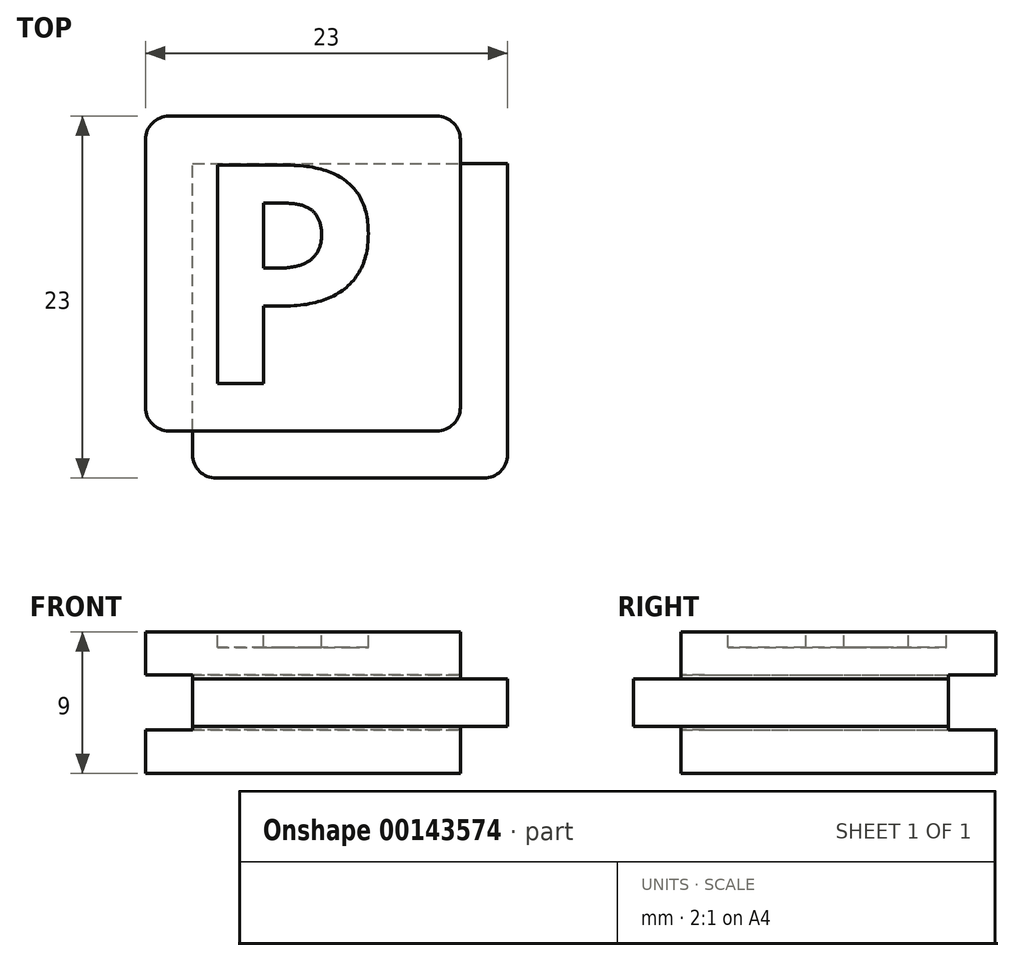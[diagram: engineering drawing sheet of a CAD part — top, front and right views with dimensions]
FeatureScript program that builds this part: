
annotation { "Feature Type Name" : "Feature", "Feature Type Description" : "" }
export const myFeature = defineFeature(function(context is Context, id is Id, definition is map)
    precondition{}
    {
        {
            var Q0;
            Q0=qCreatedBy(makeId("Front.planeOp"),FACE);
            var sketch = newSketch(context, id + "F0", { "sketchPlane" : qUnion([Q0])});
            skLineSegment(sketch, "E0.bottom", {"start": v(10, 4.5) * mm, "end": v(-10, 4.5) * mm});
            skLineSegment(sketch, "E0.top", {"start": v(10, -4.5) * mm, "end": v(-10, -4.5) * mm});
            skLineSegment(sketch, "E0.left", {"start": v(10, 4.5) * mm, "end": v(10, -4.5) * mm});
            skLineSegment(sketch, "E0.right", {"start": v(-10, 4.5) * mm, "end": v(-10, -4.5) * mm});
            skPoint(sketch, "E0.middle", {"position": v(0, 0) * mm});
            skLineSegment(sketch, "E1.bottom", {"start": v(13, 1.5) * mm, "end": v(7, 1.5) * mm});
            skLineSegment(sketch, "E1.top", {"start": v(13, -1.5) * mm, "end": v(7, -1.5) * mm});
            skLineSegment(sketch, "E1.left", {"start": v(13, 1.5) * mm, "end": v(13, -1.5) * mm});
            skLineSegment(sketch, "E1.right", {"start": v(7, 1.5) * mm, "end": v(7, -1.5) * mm});
            skPoint(sketch, "E1.middle", {"position": v(10, 0) * mm});
            skLineSegment(sketch, "E2.bottom", {"start": v(7, 1.5) * mm, "end": v(-7, 1.5) * mm});
            skLineSegment(sketch, "E2.top", {"start": v(7, -1.5) * mm, "end": v(-7, -1.5) * mm});
            skLineSegment(sketch, "E2.right", {"start": v(-7, 1.5) * mm, "end": v(-7, -1.5) * mm});
            skLineSegment(sketch, "E3.bottom", {"start": v(-7, -1.5) * mm, "end": v(-10, -1.5) * mm});
            skLineSegment(sketch, "E3.top", {"start": v(-7, 1.5) * mm, "end": v(-10, 1.5) * mm});
            skLineSegment(sketch, "E3.left", {"start": v(-7, -1.5) * mm, "end": v(-7, 1.5) * mm});
            skLineSegment(sketch, "E3.right", {"start": v(-10, -1.5) * mm, "end": v(-10, 1.5) * mm});
            skSolve(sketch);
        }
        {
            var Q0;
            {var subQ5=sQuery(id+"F0.wireOp",EDGE,"E0.bottom");Q0=makeQuery(id+"F0.imprint","IMPRINT",FACE,{"disambiguationData":[TD([[makeQuery(id+"F0.imprint","IMPRINT",EDGE,{"derivedFrom":subQ5}),1.0]])]});}
            var Q1;
            Q1=makeQuery(id+"F0.imprint","IMPRINT",FACE,{"disambiguationData":[TD([[makeQuery(id+"F0.imprint","IMPRINT",EDGE,{"derivedFrom":sQuery(id+"F0.wireOp",EDGE,"E2.bottom")}),1.0]])]});
            var Q2;
            {var subQ5=sQuery(id+"F0.wireOp",EDGE,"E1.left");Q2=makeQuery(id+"F0.imprint","IMPRINT",FACE,{"disambiguationData":[TD([[makeQuery(id+"F0.imprint","IMPRINT",EDGE,{"derivedFrom":subQ5}),-1.0]])]});}
            var Q3;
            {var subQ5=sQuery(id+"F0.wireOp",EDGE,"E1.right");Q3=makeQuery(id+"F0.imprint","IMPRINT",FACE,{"disambiguationData":[TD([[makeQuery(id+"F0.imprint","IMPRINT",EDGE,{"derivedFrom":subQ5}),1.0]])]});}
            var Q4;
            Q4=makeQuery(id+"F0.imprint","IMPRINT",FACE,{"disambiguationData":[TD([[makeQuery(id+"F0.imprint","IMPRINT",EDGE,{"derivedFrom":sQuery(id+"F0.wireOp",EDGE,"E3.bottom")}),-1.0]])]});
            var Q5;
            {var subQ5=sQuery(id+"F0.wireOp",EDGE,"E0.top");Q5=makeQuery(id+"F0.imprint","IMPRINT",FACE,{"disambiguationData":[TD([[makeQuery(id+"F0.imprint","IMPRINT",EDGE,{"derivedFrom":subQ5}),-1.0]])]});}
            extrude(context, id + "F1", {"entities" : qUnion([Q0, Q1, Q2, Q3, Q4, Q5]), "oppositeDirection" : true, "depth" : 20 * mm});
        }
        {
            var Q0;
            Q0=makeQuery(id+"F0.imprint","IMPRINT",FACE,{"disambiguationData":[TD([[makeQuery(id+"F0.imprint","IMPRINT",EDGE,{"derivedFrom":sQuery(id+"F0.wireOp",EDGE,"E3.bottom")}),-1.0]])]});
            var Q1;
            Q1=makeQuery(id+"F0.imprint","IMPRINT",FACE,{"disambiguationData":[TD([[makeQuery(id+"F0.imprint","IMPRINT",EDGE,{"derivedFrom":sQuery(id+"F0.wireOp",EDGE,"E2.bottom")}),1.0]])]});
            var Q2;
            {var subQ5=sQuery(id+"F0.wireOp",EDGE,"E1.right");Q2=makeQuery(id+"F0.imprint","IMPRINT",FACE,{"disambiguationData":[TD([[makeQuery(id+"F0.imprint","IMPRINT",EDGE,{"derivedFrom":subQ5}),1.0]])]});}
            var Q3;
            {var subQ5=sQuery(id+"F0.wireOp",EDGE,"E1.left");Q3=makeQuery(id+"F0.imprint","IMPRINT",FACE,{"disambiguationData":[TD([[makeQuery(id+"F0.imprint","IMPRINT",EDGE,{"derivedFrom":subQ5}),-1.0]])]});}
            extrude(context, id + "F2", {"entities" : qUnion([Q0, Q1, Q2, Q3]), "operationType" : NewBodyOperationType.ADD, "depth" : 3 * mm});
        }
        {
            var Q0;
            {var subQ0=sQuery(id+"F0.wireOp",EDGE,"E1.left");Q0=makeQuery(id+"F2.boolean.opBoolean","MERGE",FACE,{"derivedFrom":[makeQuery(id+"F1.opExtrude","SWEPT_FACE",FACE,{"disambiguationData":[OSD([subQ0])]}),makeQuery(id+"F2.opExtrude","SWEPT_FACE",FACE,{"disambiguationData":[OSD([subQ0])]})]});}
            var sketch = newSketch(context, id + "F3", { "sketchPlane" : qUnion([Q0])});
            skLineSegment(sketch, "E4.bottom", {"start": v(23, 1.75) * mm, "end": v(17, 1.75) * mm});
            skLineSegment(sketch, "E4.top", {"start": v(23, -1.75) * mm, "end": v(17, -1.75) * mm});
            skLineSegment(sketch, "E4.left", {"start": v(23, 1.75) * mm, "end": v(23, -1.75) * mm});
            skLineSegment(sketch, "E4.right", {"start": v(17, 1.75) * mm, "end": v(17, -1.75) * mm});
            skPoint(sketch, "E4.middle", {"position": v(20, 0) * mm});
            skSolve(sketch);
        }
        {
            var Q0;
            {var subQ1=sQuery(id+"F3.wireOp",EDGE,"E4.bottom");Q0=makeQuery(id+"F3.imprint","IMPRINT",FACE,{"disambiguationData":[TD([[makeQuery(id+"F3.imprint","IMPRINT",EDGE,{"derivedFrom":subQ1}),1.0]])]});}
            var Q1;
            {var subQ1=sQuery(id+"F0.wireOp",EDGE,"E1.left");var subQ8=makeQuery(id+"F1.opExtrude","CAP_EDGE",EDGE,{"disambiguationData":[OSD([subQ1])],"isStart":false});Q1=makeQuery(id+"F3.imprint","IMPRINT",FACE,{"disambiguationData":[TD([[makeQuery(id+"F3.imprint","IMPRINT",EDGE,{"derivedFrom":subQ8}),-1.0]])]});}
            extrude(context, id + "F4", {"entities" : qUnion([Q0, Q1]), "operationType" : NewBodyOperationType.REMOVE, "oppositeDirection" : true, "depth" : 100 * mm});
        }
        {
            var Q0;
            Q0=makeQuery(id+"F4.boolean.opBoolean","COPY",FACE,{"derivedFrom":makeQuery(id+"F4.opExtrude","SWEPT_FACE",FACE,{"disambiguationData":[OSD([sQuery(id+"F3.wireOp",EDGE,"E4.right")])]})});
            var sketch = newSketch(context, id + "F5", { "sketchPlane" : qUnion([Q0])});
            skLineSegment(sketch, "E5.bottom", {"start": v(13, 1.75) * mm, "end": v(7, 1.75) * mm});
            skLineSegment(sketch, "E5.top", {"start": v(13, -1.75) * mm, "end": v(7, -1.75) * mm});
            skLineSegment(sketch, "E5.left", {"start": v(13, 1.75) * mm, "end": v(13, -1.75) * mm});
            skLineSegment(sketch, "E5.right", {"start": v(7, 1.75) * mm, "end": v(7, -1.75) * mm});
            skPoint(sketch, "E5.middle", {"position": v(10, 0) * mm});
            skSolve(sketch);
        }
        {
            var Q0;
            {var subQ3=sQuery(id+"F5.wireOp",EDGE,"E5.left");Q0=makeQuery(id+"F5.imprint","IMPRINT",FACE,{"disambiguationData":[TD([[makeQuery(id+"F5.imprint","IMPRINT",EDGE,{"derivedFrom":subQ3}),-1.0]])]});}
            var Q1;
            {var subQ4=sQuery(id+"F5.wireOp",EDGE,"E5.right");Q1=makeQuery(id+"F5.imprint","IMPRINT",FACE,{"disambiguationData":[TD([[makeQuery(id+"F5.imprint","IMPRINT",EDGE,{"derivedFrom":subQ4}),1.0]])]});}
            extrude(context, id + "F6", {"entities" : qUnion([Q0, Q1]), "operationType" : NewBodyOperationType.REMOVE, "oppositeDirection" : true, "depth" : 100 * mm});
        }
        {
            var Q0;
            Q0=makeQuery(id+"F6.boolean.opBoolean","INTERSECT",EDGE,{"derivedFrom":[makeQuery(id+"F2.opExtrude","CAP_FACE",FACE,{"disambiguationData":[OSD([sQuery(id+"F0.wireOp",EDGE,"E1.bottom"),sQuery(id+"F0.wireOp",EDGE,"E1.top"),sQuery(id+"F0.wireOp",EDGE,"E1.left"),sQuery(id+"F0.wireOp",EDGE,"E2.bottom"),sQuery(id+"F0.wireOp",EDGE,"E2.top"),sQuery(id+"F0.wireOp",EDGE,"E3.bottom"),sQuery(id+"F0.wireOp",EDGE,"E3.top"),sQuery(id+"F0.wireOp",EDGE,"E3.right")])],"isStart":false}),makeQuery(id+"F6.opExtrude","SWEPT_FACE",FACE,{"disambiguationData":[OSD([sQuery(id+"F5.wireOp",EDGE,"E5.right")])]})]});
            var Q1;
            Q1=makeQuery(id+"F2.opExtrude","CAP_EDGE",EDGE,{"disambiguationData":[OSD([sQuery(id+"F0.wireOp",EDGE,"E1.left")])],"isStart":false});
            var Q2;
            {var subQ0=sQuery(id+"F0.wireOp",EDGE,"E0.left");Q2=makeQuery(id+"F1.opExtrude","CAP_EDGE",EDGE,{"disambiguationData":[OSD([subQ0]),TDD([makeQuery(id+"F0.imprint","IMPRINT",EDGE,{"disambiguationData":[TD([[makeQuery(id+"F0.imprint","INTERSECT",VERTEX,{"derivedFrom":[sQuery(id+"F0.wireOp",EDGE,"E0.bottom"),subQ0]}),-1.0]])],"derivedFrom":subQ0})])],"isStart":true});}
            var Q3;
            {var subQ0=sQuery(id+"F0.wireOp",EDGE,"E0.left");Q3=makeQuery(id+"F1.opExtrude","CAP_EDGE",EDGE,{"disambiguationData":[OSD([subQ0]),TDD([makeQuery(id+"F0.imprint","IMPRINT",EDGE,{"disambiguationData":[TD([[makeQuery(id+"F0.imprint","INTERSECT",VERTEX,{"derivedFrom":[sQuery(id+"F0.wireOp",EDGE,"E0.top"),subQ0]}),1.0]])],"derivedFrom":subQ0})])],"isStart":true});}
            var Q4;
            {var subQ0=sQuery(id+"F0.wireOp",EDGE,"E3.right");var subQ1=sQuery(id+"F0.wireOp",EDGE,"E0.right");var subQ3=sQuery(id+"F0.wireOp",EDGE,"E0.top");Q4=makeQuery(id+"F2.boolean.opBoolean","SPLIT",EDGE,{"disambiguationData":[TD([makeQuery(id+"F1.opExtrude","SWEPT_FACE",FACE,{"disambiguationData":[OSD([subQ3])]})])],"derivedFrom":makeQuery(id+"F1.opExtrude","CAP_EDGE",EDGE,{"disambiguationData":[OSD([subQ1,subQ0])],"isStart":true})});}
            var Q5;
            {var subQ1=sQuery(id+"F0.wireOp",EDGE,"E3.right");var subQ2=sQuery(id+"F0.wireOp",EDGE,"E0.right");var subQ3=sQuery(id+"F0.wireOp",EDGE,"E0.bottom");Q5=makeQuery(id+"F2.boolean.opBoolean","SPLIT",EDGE,{"disambiguationData":[TD([makeQuery(id+"F1.opExtrude","SWEPT_FACE",FACE,{"disambiguationData":[OSD([subQ3])]})])],"derivedFrom":makeQuery(id+"F1.opExtrude","CAP_EDGE",EDGE,{"disambiguationData":[OSD([subQ2,subQ1])],"isStart":true})});}
            var Q6;
            Q6=makeQuery(id+"F6.boolean.opBoolean","COPY",EDGE,{"derivedFrom":makeQuery(id+"F6.opExtrude","CAP_EDGE",EDGE,{"disambiguationData":[OSD([sQuery(id+"F5.wireOp",EDGE,"E5.right")])],"isStart":true})});
            var Q7;
            {var subQ0=sQuery(id+"F0.wireOp",EDGE,"E3.right");var subQ1=sQuery(id+"F0.wireOp",EDGE,"E0.right");var subQ2=sQuery(id+"F0.wireOp",EDGE,"E0.bottom");Q7=makeQuery(id+"F4.boolean.opBoolean","SPLIT",EDGE,{"disambiguationData":[TD([makeQuery(id+"F1.opExtrude","SWEPT_FACE",FACE,{"disambiguationData":[OSD([subQ2])]})])],"derivedFrom":makeQuery(id+"F1.opExtrude","CAP_EDGE",EDGE,{"disambiguationData":[OSD([subQ1,subQ0])],"isStart":false})});}
            var Q8;
            {var subQ0=sQuery(id+"F0.wireOp",EDGE,"E3.right");var subQ1=sQuery(id+"F0.wireOp",EDGE,"E0.right");var subQ2=sQuery(id+"F0.wireOp",EDGE,"E0.top");Q8=makeQuery(id+"F4.boolean.opBoolean","SPLIT",EDGE,{"disambiguationData":[TD([makeQuery(id+"F1.opExtrude","SWEPT_FACE",FACE,{"disambiguationData":[OSD([subQ2])]})])],"derivedFrom":makeQuery(id+"F1.opExtrude","CAP_EDGE",EDGE,{"disambiguationData":[OSD([subQ1,subQ0])],"isStart":false})});}
            var Q9;
            Q9=makeQuery(id+"F4.boolean.opBoolean","COPY",EDGE,{"derivedFrom":makeQuery(id+"F4.opExtrude","CAP_EDGE",EDGE,{"disambiguationData":[OSD([sQuery(id+"F3.wireOp",EDGE,"E4.right")])],"isStart":true})});
            var Q10;
            {var subQ0=sQuery(id+"F0.wireOp",EDGE,"E0.left");Q10=makeQuery(id+"F1.opExtrude","CAP_EDGE",EDGE,{"disambiguationData":[OSD([subQ0]),TDD([makeQuery(id+"F0.imprint","IMPRINT",EDGE,{"disambiguationData":[TD([[makeQuery(id+"F0.imprint","INTERSECT",VERTEX,{"derivedFrom":[sQuery(id+"F0.wireOp",EDGE,"E0.bottom"),subQ0]}),-1.0]])],"derivedFrom":subQ0})])],"isStart":false});}
            var Q11;
            {var subQ0=sQuery(id+"F0.wireOp",EDGE,"E0.left");Q11=makeQuery(id+"F1.opExtrude","CAP_EDGE",EDGE,{"disambiguationData":[OSD([subQ0]),TDD([makeQuery(id+"F0.imprint","IMPRINT",EDGE,{"disambiguationData":[TD([[makeQuery(id+"F0.imprint","INTERSECT",VERTEX,{"derivedFrom":[sQuery(id+"F0.wireOp",EDGE,"E0.top"),subQ0]}),1.0]])],"derivedFrom":subQ0})])],"isStart":false});}
            fillet(context, id + "F7", {"entities" : qUnion([Q0, Q1, Q2, Q3, Q4, Q5, Q6, Q7, Q8, Q9, Q10, Q11]), "radius" : 1.5 * mm, "tangentPropagation" : true, "allowEdgeOverflow" : false});
        }
        {
            var Q0;
            Q0=makeQuery(id+"F1.opExtrude","SWEPT_FACE",FACE,{"disambiguationData":[OSD([sQuery(id+"F0.wireOp",EDGE,"E0.bottom")])]});
            var sketch = newSketch(context, id + "F8", { "sketchPlane" : qUnion([Q0])});
            skText(sketch, "E6", { "text": "P", "fontName": "OpenSans-Bold.ttf"});
            skLineSegment(sketch, "E7.0", {"start": v(9.3, 3) * mm, "end": v(-11.07, 3) * mm});
            const initialGuessF8  = {"E6": [-0.00718, 0.003, 1, 0, 0.014]};
            skSetInitialGuess(sketch, initialGuessF8);
            skSolve(sketch);
        }
        {
            var Q0;
            Q0=makeQuery(id+"F8.imprint","IMPRINT",FACE,{"disambiguationData":[TD([[makeQuery(id+"F8.imprint","IMPRINT",EDGE,{"derivedFrom":sQuery(id+"F8.wireOp",EDGE,"E6.sketch_text.stroke-0")}),-1.0]])]});
            extrude(context, id + "F9", {"entities" : qUnion([Q0]), "operationType" : NewBodyOperationType.REMOVE, "oppositeDirection" : true, "depth" : 1 * mm});
        }
    });
